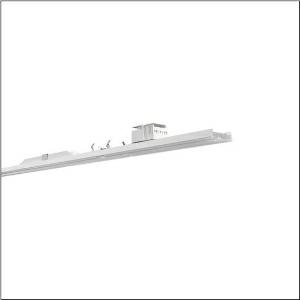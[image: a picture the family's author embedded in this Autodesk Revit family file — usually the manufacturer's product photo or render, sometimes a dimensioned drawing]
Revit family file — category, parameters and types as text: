
# Revit family: licross_r__11_recessed_ho_51tl12dn4dxl_7c2f
name_source: partatom
category: Lighting Fixtures
units: mm (PartAtom-declared; Revit-internal decimal feet)

## family parameters
Cut with Voids When Loaded = No
Host = Face
Light Source = No
Part Type = Normal
Room Calculation Point = No
Round Connector Dimension = Use Diameter
Shared = No

## types (1)
- --- (1 x LED, 13000 lm, 76 W, 4000K)
    Apparent Load = 76 VA
    CIE Flux Codes = 66 91 98 100 100
    Color Rendering = 80
    Color Temperature = 4000K
    Default Elevation = 1800 mm
    Description = Licross® 11 Recessed HOluminaire insert, length: 1.500mm, width: 66mm, height: 67mm, LED rated luminous flux: 13.000lm, light colour: 840, control gear: DALI 2, control gear: ECG DALI, with plug, 5-pole, with phase selection, mains connection: 220..240V, AC, 50/60Hz, halogen-free wiring, primary optical cover: cover, of PMMA, light emission: direct distribution, protection rating (complete): IP40, insulation class (complete): insulation class I (protective earthing), certification: CE, ENEC, VDE, protection symbol: D if used in an environment without relevant dust loads with corresponding accessories, permissible ambient temperature for indoor applications: -25..+35°C, reducing of maximum allowable ambient temperature of 5°C with ceiling mounting, corresponds to IFS (International Featured Standards) requirements for safety and quality in the food industry, packaging unit: 1 piece
    Height = 58 mm
    Lamp = 1 x LED
    Lamp Light Flux = 13000 lm
    Lamp Power = 76 W
    Lamp count = 1
    Length = 1500 mm
    Luminous efficacy = 171 lm/W
    Manufacturer = Siteco
    ModVariant = No
    Model = 51TL12DN4DXL
    Mounting Place = Ceiling
    Mounting Type = Pendant
    Number of Poles = 1
    OnlyDefault = Yes
    Power Factor = 1
    Product Name = Licross® 11 Recessed HO
    Product group = luminaire insert
    ProductGroupID = 902
    Protection Class = Protection class I
    Protection Degree = IP 40
    RLX_Detail_Level = 1
    RlxData = <blob elided: 22081 chars, md5=da4c9f84>
    Socket = socket
    Standby Power = 0 W
    System Light Flux = 13000 lm
    System Power = 76 W
    Type Comments = factory setting: luminous flux: 100 % | dim-lin: 254 | 430 mA
    Type Image = l_1266722.jpg
    URL = http://relux.com
    VarID = @adj_138975
    Voltage = 0 V
    Weight = 0.00 kg
    Width = 66 mm

## geometry (parser evidence)
native form markers: Blend x4, Sweep x13
no freeform markers — native parametric forms only
